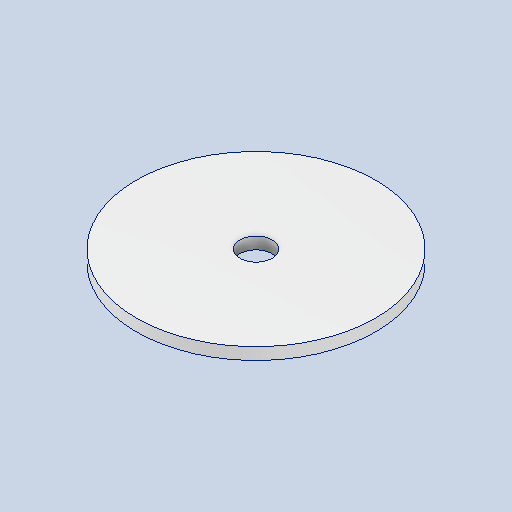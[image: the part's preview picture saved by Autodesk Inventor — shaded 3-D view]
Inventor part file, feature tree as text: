
AUTODESK INVENTOR PART (.ipt)
format: ipt  version: 2023.1 (Build 271208000, 208)  size: 215,040 bytes
history: native  units: in
note: dims shown in document units (in); Inventor stores cm internally (conversion verified against a paired STEP export)
features: extrude x2
ambient origin geometry x8: Origin, YZ Plane, XZ Plane, XY Plane, X Axis, Y Axis, Z Axis, Center Point
bodies: Solid1 (feature_tree)
feature tree (2):
  extrude  "Extrusion1"  Depth=0.1575in TaperAngle=0.0deg
  extrude  "Extrusion3"  Depth=3.1496in
